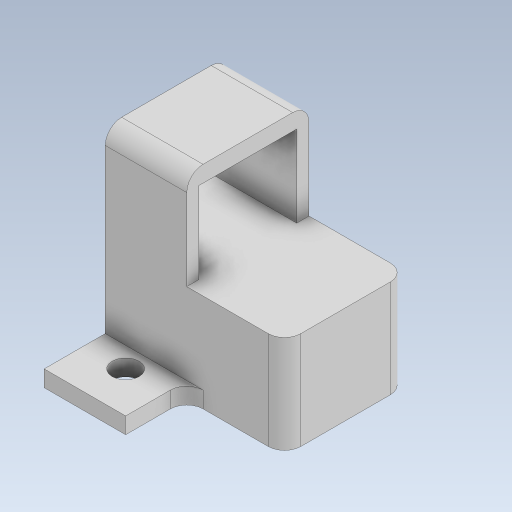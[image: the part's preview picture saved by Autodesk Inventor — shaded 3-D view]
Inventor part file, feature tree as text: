
AUTODESK INVENTOR PART (.ipt)
format: ipt  version: 2023.5 (Build 275446000, 446)  size: 155,648 bytes
history: native  units: mm
features: extrude x4, sketch x2, fillet x1
ambient origin geometry x8: Origin, YZ Plane, XZ Plane, XY Plane, X Axis, Y Axis, Z Axis, Center Point
bodies: Solid1 (feature_tree)
feature tree (7):
  sketch  "Sketch1"  dims[d3=3.3mm d6=3.3mm]
  extrude  "Extrusion1"  Depth=3.3mm
  extrude  "Extrusion2"  Depth=24.0mm TaperAngle=0.0deg
  sketch  "Sketch2"  dims[d9=2.0mm d10=0.0mm d11=24.0mm d12=0.0mm d13=2.0mm d14=10.0mm d15=24.0mm d16=0.0mm d17=12.0mm d18=0.0mm d19=2.0mm]
  extrude  "Extrusion3"  Depth=2.0mm
  extrude  "Extrusion4"  Depth=10.0mm
  fillet  "Fillet1"  Radius=24.0mm
